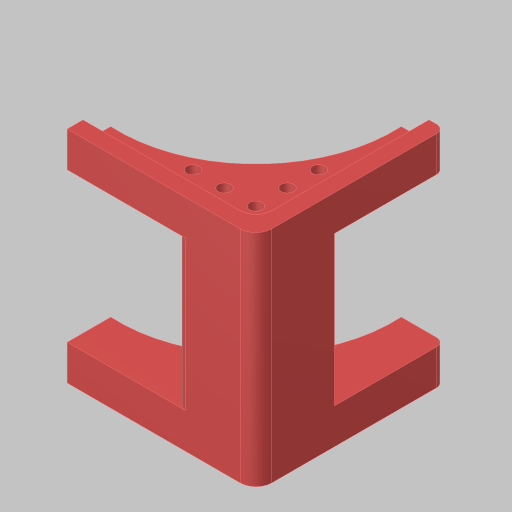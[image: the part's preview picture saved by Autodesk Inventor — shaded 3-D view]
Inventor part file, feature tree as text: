
AUTODESK INVENTOR PART (.ipt)
format: ipt  version: 2023.5 (Build 275446000, 446)  size: 281,088 bytes
history: native  units: in
note: dims shown in document units (in); Inventor stores cm internally (conversion verified against a paired STEP export)
features: extrude x8, sketch x8, projected_geometry x5, other x4, fillet x2, loft x2, hole x1
ambient origin geometry x8: Origin, YZ Plane, XZ Plane, XY Plane, X Axis, Y Axis, Z Axis, Center Point
bodies: Solid1 (feature_tree)
feature tree (30):
  extrude  "Extrusion1"  Depth=1.25in
  extrude  "Extrusion2"  Depth=0.3125in
  sketch  "Sketch4"  dims[d6=0.5in d7=0.5in]
  extrude  "Extrusion3"  Depth=0.5in
  extrude  "Extrusion4"  Depth=0.5in
  sketch  "Sketch5"  dims[d8=0.5in d9=0.5in]
  extrude  "Extrusion6"  Depth=0.3125in TaperAngle=0.0deg
  extrude  "Extrusion5"  Depth=0.5in
  sketch  "Sketch9"  dims[d13=0.5in d14=0.5in d15=0.5in]
  fillet  "Fillet2"  Radius=0.5in
  hole  "Hole1"  [1 undecoded]
  extrude  "Extrusion9"  Depth=0.125in
  sketch  "Sketch12"  dims[d18=0.1875in d19=0.0in d20=0.125in d21=0.125in d22=0.0in d23=0.25in d24=0.25in d25=1.75in d26=0.0in d27=1.75in d28=0.0in d35=0.5in d36=0.5in d37=0.5in d38=0.5in d39=0.5in d40=0.5in d41=0.25in d43=0.201in d44=0.38in d45=0.385in d46=0.25in d47=0.5635in d48=1.0in d49=0.8108in d53=0.3333in d54=0.3333in d55=0.3333in d56=0.25in d57=0.0in d60=0.25in d62=2.125in d63=2.125in d64=4.375in d68=0.0in d69=90.0deg d70=0.0in d71=90.0deg d72=0.0in d73=90.0deg d74=0.0in d75=90.0deg d76=0.0in d77=0.0in d78=0.125in]
  loft  "Loft1"
  loft  "Loft2"
  extrude  "Extrusion11"  Depth=0.25in
  fillet  "Fillet7"  Radius=1.75in
  sketch  "Sketch2"  dims[d0=1.25in d1=1.25in]
  sketch  "Sketch3"  dims[d2=2.998in d3=0.0in d4=0.3125in]
  sketch  "Sketch6"  dims[d10=0.25in d11=0.3125in d12=0.0in]
  sketch  "Sketch11"  dims[d16=0.5in d17=0.25in]
  other  "Edges1"
  other  "Edges2"
  other  "Edges3"
  other  "Edges4"
  projected_geometry  "Project Cut Edges1"
  projected_geometry  "Project Cut Edges2"
  projected_geometry  "Project Cut Edges3"
  projected_geometry  "Project Cut Edges4"
  projected_geometry  "Project Cut Edges7"
note: 1 required parameter value undecoded (feature->parameter linkage not recoverable at this tier; creation-order binding heuristic only, values carry confidence <= 0.55)
